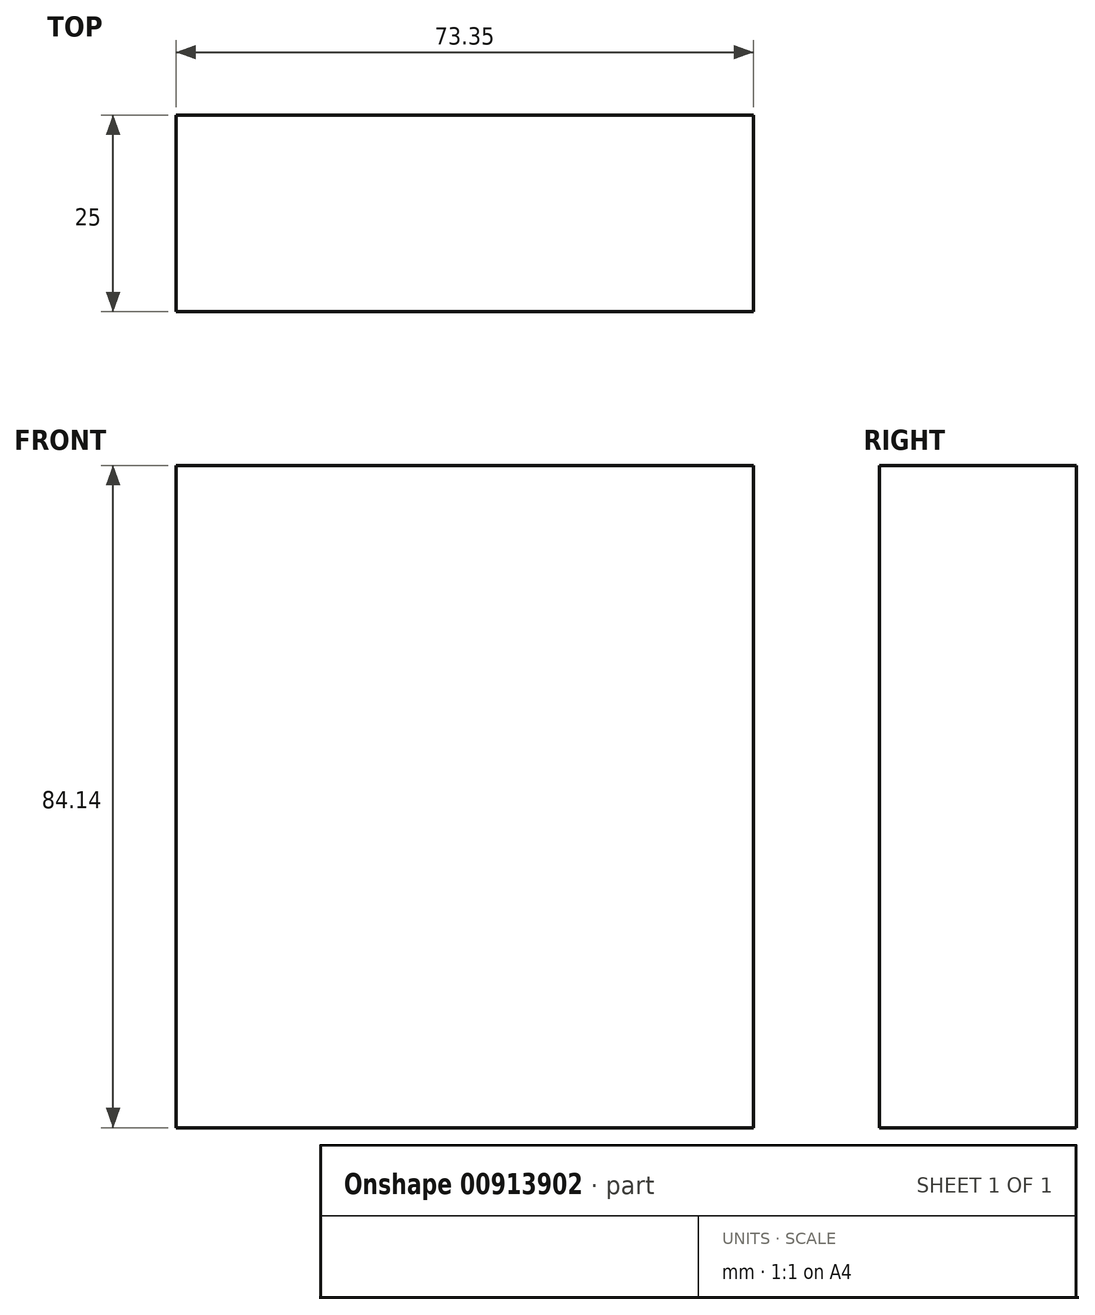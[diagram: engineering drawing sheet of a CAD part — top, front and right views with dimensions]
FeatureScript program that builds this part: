
annotation { "Feature Type Name" : "Feature", "Feature Type Description" : "" }
export const myFeature = defineFeature(function(context is Context, id is Id, definition is map)
    precondition{}
    {
        {
            var Q0;
            Q0=qCreatedBy(makeId("Front.planeOp"),FACE);
            var sketch = newSketch(context, id + "F0", { "sketchPlane" : qUnion([Q0])});
            skLineSegment(sketch, "E0.bottom", {"start": v(-167.96, -52.54) * mm, "end": v(-94.6, -52.54) * mm});
            skLineSegment(sketch, "E0.top", {"start": v(-167.96, 31.6) * mm, "end": v(-94.6, 31.6) * mm});
            skLineSegment(sketch, "E0.left", {"start": v(-167.96, -52.54) * mm, "end": v(-167.96, 31.6) * mm});
            skLineSegment(sketch, "E0.right", {"start": v(-94.6, -52.54) * mm, "end": v(-94.6, 31.6) * mm});
            skPoint(sketch, "E0.middle", {"position": v(-131.28, -10.47) * mm});
            skSolve(sketch);
        }
        {
            var Q0;
            Q0=makeQuery(id+"F0.imprint","IMPRINT",FACE,{"disambiguationData":[TD([[makeQuery(id+"F0.imprint","IMPRINT",EDGE,{"derivedFrom":sQuery(id+"F0.wireOp",EDGE,"E0.bottom")}),1.0]])]});
            extrude(context, id + "F1", {"entities" : qUnion([Q0]), "depth" : 25 * mm, "offsetDistance" : 25 * mm});
        }
    });
